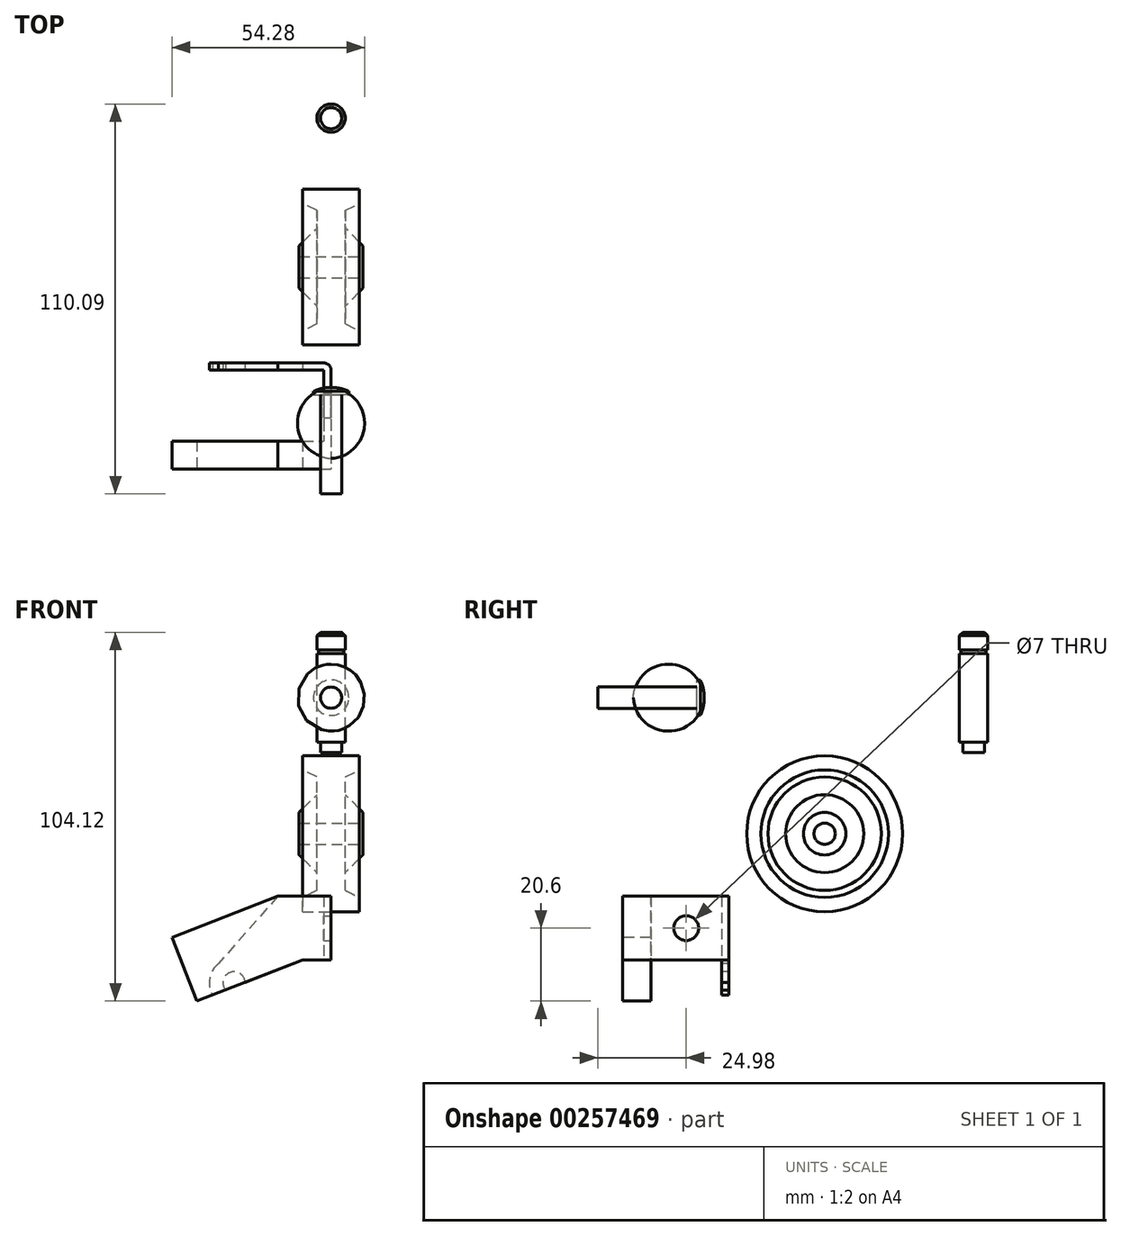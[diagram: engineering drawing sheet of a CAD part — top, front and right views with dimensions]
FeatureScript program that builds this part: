
annotation { "Feature Type Name" : "Feature", "Feature Type Description" : "" }
export const myFeature = defineFeature(function(context is Context, id is Id, definition is map)
    precondition{}
    {
        {
            var Q0;
            Q0=qCreatedBy(makeId("Front.planeOp"),FACE);
            var sketch = newSketch(context, id + "F0", { "sketchPlane" : qUnion([Q0])});
            skLineSegment(sketch, "E0", {"start": v(-8, 22) * mm, "end": v(8, 22) * mm});
            skLineSegment(sketch, "E1", {"start": v(-8, 22) * mm, "end": v(-8, 18) * mm});
            skLineSegment(sketch, "E2", {"start": v(8, 22) * mm, "end": v(8, 18) * mm});
            skLineSegment(sketch, "E3", {"start": v(-9, 3) * mm, "end": v(9, 3) * mm});
            skLineSegment(sketch, "E4", {"start": v(-9, 3) * mm, "end": v(-9, 6) * mm});
            skLineSegment(sketch, "E5", {"start": v(9, 3) * mm, "end": v(9, 6) * mm});
            skLineSegment(sketch, "E6", {"start": v(0, 0) * mm, "end": v(-4, 0) * mm});
            skLineSegment(sketch, "E7", {"start": v(0, 0) * mm, "end": v(4, 0) * mm});
            skLineSegment(sketch, "E8", {"start": v(-4, 11) * mm, "end": v(-4, 16) * mm});
            skLineSegment(sketch, "E9", {"start": v(4, 11) * mm, "end": v(4, 16) * mm});
            skLineSegment(sketch, "E10", {"start": v(-9, 6) * mm, "end": v(-4, 11) * mm});
            skLineSegment(sketch, "E11", {"start": v(-4, 16) * mm, "end": v(-8, 18) * mm});
            skLineSegment(sketch, "E12", {"start": v(4, 16) * mm, "end": v(8, 18) * mm});
            skLineSegment(sketch, "E13", {"start": v(4, 11) * mm, "end": v(9, 6) * mm});
            skSolve(sketch);
        }
        {
            var Q0;
            Q0=makeQuery(id+"F0.imprint","IMPRINT",FACE,{"disambiguationData":[TD([[makeQuery(id+"F0.imprint","IMPRINT",EDGE,{"derivedFrom":sQuery(id+"F0.wireOp",EDGE,"E0")}),-1.0]])]});
            var Q1;
            Q1=sQuery(id+"F0.wireOp",EDGE,"E6");
            revolve(context, id + "F1", {"entities" : qUnion([Q0]), "axis" : qUnion([Q1]), "revolveType" : RevolveType.FULL});
        }
        {
            var Q0;
            Q0=qCreatedBy(makeId("Right.planeOp"),FACE);
            var sketch = newSketch(context, id + "F2", { "sketchPlane" : qUnion([Q0])});
            skLineSegment(sketch, "E14", {"start": v(-64.05, 35.4) * mm, "end": v(-64.05, 38.4) * mm});
            skLineSegment(sketch, "E15", {"start": v(-64.05, 35.4) * mm, "end": v(-36.05, 35.4) * mm});
            skLineSegment(sketch, "E16", {"start": v(-64.05, 38.4) * mm, "end": v(-34.05, 38.4) * mm});
            skLineSegment(sketch, "E17", {"start": v(-36.08, 38.4) * mm, "end": v(-36.08, 33.4) * mm});
            skLineSegment(sketch, "E18", {"start": v(-36.08, 33.4) * mm, "end": v(-35.08, 33.4) * mm});
            skLineSegment(sketch, "E19", {"start": v(-36.08, 38.4) * mm, "end": v(-35.08, 38.4) * mm});
            skLineSegment(sketch, "E20", {"start": v(-35.08, 38.4) * mm, "end": v(-35.08, 33.4) * mm});
            skArc(sketch, "E21", {"start": v(-35.08, 33.4) * mm, "mid": v(-34.24, 35.83) * mm, "end": v(-34.05, 38.4) * mm});
            skSolve(sketch);
        }
        {
            var Q0;
            {var subQ2=sQuery(id+"F2.wireOp",EDGE,"E20");Q0=makeQuery(id+"F2.imprint","IMPRINT",FACE,{"disambiguationData":[TD([[makeQuery(id+"F2.imprint","IMPRINT",EDGE,{"derivedFrom":subQ2}),1.0]])]});}
            var Q1;
            {var subQ1=sQuery(id+"F2.wireOp",EDGE,"E18");Q1=makeQuery(id+"F2.imprint","IMPRINT",FACE,{"disambiguationData":[TD([[makeQuery(id+"F2.imprint","IMPRINT",EDGE,{"derivedFrom":subQ1}),1.0]])]});}
            var Q2;
            {var subQ0=sQuery(id+"F2.wireOp",EDGE,"E14");Q2=makeQuery(id+"F2.imprint","IMPRINT",FACE,{"disambiguationData":[TD([[makeQuery(id+"F2.imprint","IMPRINT",EDGE,{"derivedFrom":subQ0}),-1.0]])]});}
            var Q3;
            Q3=sQuery(id+"F2.wireOp",EDGE,"E16");
            revolve(context, id + "F3", {"entities" : qUnion([Q0, Q1, Q2]), "axis" : qUnion([Q3]), "revolveType" : RevolveType.FULL});
        }
        {
            var Q0;
            Q0=qCreatedBy(makeId("Right.planeOp"),FACE);
            var sketch = newSketch(context, id + "F4", { "sketchPlane" : qUnion([Q0])});
            skLineSegment(sketch, "E22", {"start": v(42.04, 56.87) * mm, "end": v(42.04, 22.87) * mm});
            skLineSegment(sketch, "E23", {"start": v(42.04, 22.87) * mm, "end": v(45.04, 22.87) * mm});
            skLineSegment(sketch, "E24", {"start": v(45.04, 22.87) * mm, "end": v(45.04, 25.87) * mm});
            skLineSegment(sketch, "E25", {"start": v(45.04, 25.87) * mm, "end": v(46.04, 25.87) * mm});
            skLineSegment(sketch, "E26", {"start": v(46.04, 25.87) * mm, "end": v(46.04, 50.87) * mm});
            skLineSegment(sketch, "E27", {"start": v(46.04, 50.87) * mm, "end": v(42.04, 50.87) * mm});
            skLineSegment(sketch, "E28", {"start": v(42.04, 50.87) * mm, "end": v(45.54, 50.87) * mm});
            skLineSegment(sketch, "E29", {"start": v(45.54, 50.87) * mm, "end": v(45.54, 51.87) * mm});
            skLineSegment(sketch, "E30", {"start": v(42.04, 51.87) * mm, "end": v(46.04, 51.87) * mm});
            skLineSegment(sketch, "E31", {"start": v(46.04, 51.87) * mm, "end": v(46.04, 55.87) * mm});
            skLineSegment(sketch, "E32", {"start": v(46.04, 55.87) * mm, "end": v(42.04, 55.87) * mm});
            skLineSegment(sketch, "E33", {"start": v(42.04, 56.87) * mm, "end": v(45.04, 56.87) * mm});
            skLineSegment(sketch, "E34", {"start": v(45.04, 56.87) * mm, "end": v(46.04, 55.87) * mm});
            skSolve(sketch);
        }
        {
            var Q0;
            Q0 = qSketchRegion(id + "F4", true);
            var Q1;
            Q1=sQuery(id+"F4.wireOp",EDGE,"E22");
            revolve(context, id + "F5", {"entities" : qUnion([Q0]), "axis" : qUnion([Q1]), "revolveType" : RevolveType.FULL});
        }
        {
            var Q0;
            Q0=qCreatedBy(makeId("Right.planeOp"),FACE);
            var sketch = newSketch(context, id + "F6", { "sketchPlane" : qUnion([Q0])});
            skLineSegment(sketch, "E35", {"start": v(-27.07, -17.65) * mm, "end": v(-51.07, -17.65) * mm});
            skLineSegment(sketch, "E36", {"start": v(-27.07, -17.65) * mm, "end": v(-27.07, -35.65) * mm});
            skLineSegment(sketch, "E37", {"start": v(-27.07, -35.65) * mm, "end": v(-51.07, -35.65) * mm});
            skLineSegment(sketch, "E38", {"start": v(-51.07, -35.65) * mm, "end": v(-51.07, -17.65) * mm});
            skLineSegment(sketch, "E39", {"start": v(-27.07, -17.65) * mm, "end": v(-29.07, -17.65) * mm});
            skLineSegment(sketch, "E40", {"start": v(-29.07, -17.65) * mm, "end": v(-29.07, -35.65) * mm});
            skLineSegment(sketch, "E41", {"start": v(-51.07, -17.65) * mm, "end": v(-49.07, -17.65) * mm});
            skLineSegment(sketch, "E42", {"start": v(-49.07, -17.65) * mm, "end": v(-49.07, -35.65) * mm});
            skSolve(sketch);
        }
        {
            var Q0;
            Q0=makeQuery(id+"F6.imprint","IMPRINT",FACE,{"disambiguationData":[TD([[makeQuery(id+"F6.imprint","IMPRINT",EDGE,{"derivedFrom":sQuery(id+"F6.wireOp",EDGE,"E35")}),1.0]])]});
            var Q1;
            {var subQ0=sQuery(id+"F6.wireOp",EDGE,"E36");Q1=makeQuery(id+"F6.imprint","IMPRINT",FACE,{"disambiguationData":[TD([[makeQuery(id+"F6.imprint","IMPRINT",EDGE,{"derivedFrom":subQ0}),-1.0]])]});}
            var Q2;
            {var subQ0=sQuery(id+"F6.wireOp",EDGE,"E38");Q2=makeQuery(id+"F6.imprint","IMPRINT",FACE,{"disambiguationData":[TD([[makeQuery(id+"F6.imprint","IMPRINT",EDGE,{"derivedFrom":subQ0}),-1.0]])]});}
            extrude(context, id + "F7", {"entities" : qUnion([Q0, Q1, Q2]), "oppositeDirection" : true, "depth" : 2 * mm});
        }
        {
            var Q0;
            Q0=makeQuery(id+"F7.opExtrude","CAP_FACE",FACE,{"disambiguationData":[OSD([sQuery(id+"F6.wireOp",EDGE,"E35"),sQuery(id+"F6.wireOp",EDGE,"E36"),sQuery(id+"F6.wireOp",EDGE,"E37"),sQuery(id+"F6.wireOp",EDGE,"E38"),sQuery(id+"F6.wireOp",EDGE,"E39"),sQuery(id+"F6.wireOp",EDGE,"E41")])],"isStart":false});
            var sketch = newSketch(context, id + "F8", { "sketchPlane" : qUnion([Q0])});
            skLineSegment(sketch, "E43.bottom", {"start": v(27.07, -17.65) * mm, "end": v(29.07, -17.65) * mm});
            skLineSegment(sketch, "E43.top", {"start": v(27.07, -35.65) * mm, "end": v(29.07, -35.65) * mm});
            skLineSegment(sketch, "E43.left", {"start": v(27.07, -17.65) * mm, "end": v(27.07, -35.65) * mm});
            skLineSegment(sketch, "E43.right", {"start": v(29.07, -17.65) * mm, "end": v(29.07, -35.65) * mm});
            skLineSegment(sketch, "E44.bottom", {"start": v(51.07, -17.65) * mm, "end": v(49.07, -17.65) * mm});
            skLineSegment(sketch, "E44.top", {"start": v(51.07, -35.65) * mm, "end": v(49.07, -35.65) * mm});
            skLineSegment(sketch, "E44.left", {"start": v(51.07, -17.65) * mm, "end": v(51.07, -35.65) * mm});
            skLineSegment(sketch, "E44.right", {"start": v(49.07, -17.65) * mm, "end": v(49.07, -35.65) * mm});
            skSolve(sketch);
        }
        {
            var Q0;
            Q0=makeQuery(id+"F8.imprint","IMPRINT",FACE,{"disambiguationData":[TD([[makeQuery(id+"F8.imprint","IMPRINT",EDGE,{"derivedFrom":sQuery(id+"F8.wireOp",EDGE,"E43.bottom")}),-1.0]])]});
            var Q1;
            Q1=makeQuery(id+"F8.imprint","IMPRINT",FACE,{"disambiguationData":[TD([[makeQuery(id+"F8.imprint","IMPRINT",EDGE,{"derivedFrom":sQuery(id+"F8.wireOp",EDGE,"E44.bottom")}),-1.0]])]});
            extrude(context, id + "F9", {"entities" : qUnion([Q0, Q1]), "operationType" : NewBodyOperationType.ADD, "depth" : 13 * mm});
        }
        {
            var Q0;
            Q0=makeQuery(id+"F9.boolean.opBoolean","MERGE",FACE,{"derivedFrom":[makeQuery(id+"F7.opExtrude","SWEPT_FACE",FACE,{"disambiguationData":[OSD([sQuery(id+"F6.wireOp",EDGE,"E38")])]}),makeQuery(id+"F9.opExtrude","SWEPT_FACE",FACE,{"disambiguationData":[OSD([sQuery(id+"F8.wireOp",EDGE,"E44.left")])]})]});
            var sketch = newSketch(context, id + "F10", { "sketchPlane" : qUnion([Q0])});
            skLineSegment(sketch, "E45", {"start": v(0, -35.65) * mm, "end": v(-8, -35.65) * mm});
            skLineSegment(sketch, "E46", {"start": v(-8, -35.65) * mm, "end": v(-15, -17.65) * mm});
            skSolve(sketch);
        }
        {
            var Q0;
            {var subQ0=sQuery(id+"F10.wireOp",EDGE,"E46");Q0=makeQuery(id+"F10.imprint","IMPRINT",FACE,{"disambiguationData":[TD([[makeQuery(id+"F10.imprint","IMPRINT",EDGE,{"derivedFrom":subQ0}),1.0]])]});}
            extrude(context, id + "F11", {"entities" : qUnion([Q0]), "operationType" : NewBodyOperationType.REMOVE, "oppositeDirection" : true, "depth" : 24 * mm});
        }
        {
            var Q0;
            Q0=makeQuery(id+"F11.boolean.opBoolean","COPY",FACE,{"disambiguationData":[TD([makeQuery(id+"F7.opExtrude","SWEPT_FACE",FACE,{"disambiguationData":[OSD([sQuery(id+"F6.wireOp",EDGE,"E36")])]})])],"derivedFrom":makeQuery(id+"F11.opExtrude","SWEPT_FACE",FACE,{"disambiguationData":[OSD([sQuery(id+"F10.wireOp",EDGE,"E46")])]})});
            var Q1;
            Q1=makeQuery(id+"F11.boolean.opBoolean","COPY",FACE,{"disambiguationData":[TD([makeQuery(id+"F7.opExtrude","SWEPT_FACE",FACE,{"disambiguationData":[OSD([sQuery(id+"F6.wireOp",EDGE,"E38")])]})])],"derivedFrom":makeQuery(id+"F11.opExtrude","SWEPT_FACE",FACE,{"disambiguationData":[OSD([sQuery(id+"F10.wireOp",EDGE,"E46")])]})});
            extrude(context, id + "F12", {"entities" : qUnion([Q0, Q1]), "operationType" : NewBodyOperationType.ADD, "depth" : 32 * mm});
        }
        {
            var Q0;
            {var subQ0=sQuery(id+"F8.wireOp",EDGE,"E44.top");var subQ1=sQuery(id+"F6.wireOp",EDGE,"E38");var subQ2=sQuery(id+"F6.wireOp",EDGE,"E37");var subQ3=sQuery(id+"F8.wireOp",EDGE,"E44.left");var subQ4=sQuery(id+"F10.wireOp",EDGE,"E46");var subQ5=sQuery(id+"F10.wireOp",EDGE,"E45");Q0=makeQuery(id+"F12.opExtrude","SWEPT_FACE",FACE,{"disambiguationData":[OSD([subQ2,subQ1,subQ0,subQ3,subQ5,subQ4]),TDD([makeQuery(id+"F11.boolean.opBoolean","COPY",EDGE,{"disambiguationData":[TD([makeQuery(id+"F7.opExtrude","SWEPT_FACE",FACE,{"disambiguationData":[OSD([subQ1])]})])],"derivedFrom":makeQuery(id+"F11.opExtrude","SWEPT_EDGE",EDGE,{"disambiguationData":[OSD([subQ2,subQ1,subQ0,subQ3,subQ5,subQ4])]})})])]});}
            var Q1;
            {var subQ0=sQuery(id+"F6.wireOp",EDGE,"E37");var subQ1=sQuery(id+"F8.wireOp",EDGE,"E44.top");var subQ2=sQuery(id+"F10.wireOp",EDGE,"E46");var subQ3=sQuery(id+"F10.wireOp",EDGE,"E45");var subQ4=sQuery(id+"F8.wireOp",EDGE,"E44.left");var subQ5=sQuery(id+"F6.wireOp",EDGE,"E38");Q1=makeQuery(id+"F12.opExtrude","SWEPT_FACE",FACE,{"disambiguationData":[OSD([subQ0,subQ5,subQ1,subQ4,subQ3,subQ2]),TDD([makeQuery(id+"F11.boolean.opBoolean","COPY",EDGE,{"disambiguationData":[TD([makeQuery(id+"F7.opExtrude","SWEPT_FACE",FACE,{"disambiguationData":[OSD([sQuery(id+"F6.wireOp",EDGE,"E36")])]})])],"derivedFrom":makeQuery(id+"F11.opExtrude","SWEPT_EDGE",EDGE,{"disambiguationData":[OSD([subQ0,subQ5,subQ1,subQ4,subQ3,subQ2])]})})])]});}
            extrude(context, id + "F13", {"entities" : qUnion([Q0, Q1]), "operationType" : NewBodyOperationType.ADD, "depth" : 6 * mm});
        }
        {
            var Q0;
            {var subQ0=sQuery(id+"F10.wireOp",EDGE,"E46");Q0=makeQuery(id+"F12.boolean.opBoolean","MERGE",FACE,{"derivedFrom":[makeQuery(id+"F9.boolean.opBoolean","MERGE",FACE,{"derivedFrom":[makeQuery(id+"F7.opExtrude","SWEPT_FACE",FACE,{"disambiguationData":[OSD([sQuery(id+"F6.wireOp",EDGE,"E38")])]}),makeQuery(id+"F9.opExtrude","SWEPT_FACE",FACE,{"disambiguationData":[OSD([sQuery(id+"F8.wireOp",EDGE,"E44.left")])]})]}),makeQuery(id+"F12.opExtrude","SWEPT_FACE",FACE,{"disambiguationData":[OSD([subQ0]),TDD([makeQuery(id+"F11.boolean.opBoolean","COPY",EDGE,{"derivedFrom":makeQuery(id+"F11.opExtrude","CAP_EDGE",EDGE,{"disambiguationData":[OSD([subQ0])],"isStart":true})})])]})]});}
            var sketch = newSketch(context, id + "F14", { "sketchPlane" : qUnion([Q0])});
            skPoint(sketch, "E47.first.point", {"position": v(-40.24, -41.04) * mm});
            skPoint(sketch, "E47.third.point", {"position": v(-30.84, -29.93) * mm});
            skLineSegment(sketch, "E48", {"start": v(-15, -17.65) * mm, "end": v(-31.73, -36.63) * mm});
            skLineSegment(sketch, "E49", {"start": v(-8, -35.65) * mm, "end": v(-22.05, -46.58) * mm});
            skCircle(sketch, "E50", {"center": v(-27.38, -42.09) * mm, "radius": 6.98 * mm});
            skPoint(sketch, "E50.third.point", {"position": v(-21.22, -38.82) * mm});
            skCircle(sketch, "E51", {"center": v(-27.38, -42.09) * mm, "radius": 3.12 * mm});
            skSolve(sketch);
        }
        {
            var Q0;
            {var subQ4=sQuery(id+"F14.wireOp",EDGE,"E48");Q0=makeQuery(id+"F14.imprint","IMPRINT",FACE,{"disambiguationData":[TD([[makeQuery(id+"F14.imprint","IMPRINT",EDGE,{"derivedFrom":subQ4}),-1.0]])]});}
            var Q1;
            Q1=makeQuery(id+"F14.imprint","IMPRINT",FACE,{"disambiguationData":[TD([[makeQuery(id+"F14.imprint","IMPRINT",EDGE,{"derivedFrom":sQuery(id+"F14.wireOp",EDGE,"E51")}),1.0]])]});
            extrude(context, id + "F15", {"entities" : qUnion([Q0, Q1]), "operationType" : NewBodyOperationType.REMOVE, "oppositeDirection" : true, "depth" : 24 * mm});
        }
        {
            var Q0;
            Q0=makeQuery(id+"F7.opExtrude","CAP_FACE",FACE,{"disambiguationData":[OSD([sQuery(id+"F6.wireOp",EDGE,"E35"),sQuery(id+"F6.wireOp",EDGE,"E36"),sQuery(id+"F6.wireOp",EDGE,"E37"),sQuery(id+"F6.wireOp",EDGE,"E38"),sQuery(id+"F6.wireOp",EDGE,"E39"),sQuery(id+"F6.wireOp",EDGE,"E41")])],"isStart":true});
            var sketch = newSketch(context, id + "F16", { "sketchPlane" : qUnion([Q0])});
            skLineSegment(sketch, "E52", {"start": v(-27.07, -17.65) * mm, "end": v(-39.07, -17.65) * mm});
            skLineSegment(sketch, "E53", {"start": v(-39.07, -17.65) * mm, "end": v(-39.07, -26.65) * mm});
            skCircle(sketch, "E54", {"center": v(-39.07, -26.65) * mm, "radius": 3.5 * mm});
            skSolve(sketch);
        }
        {
            var Q0;
            Q0=makeQuery(id+"F16.imprint","IMPRINT",FACE,{"disambiguationData":[TD([[makeQuery(id+"F16.imprint","IMPRINT",EDGE,{"derivedFrom":sQuery(id+"F16.wireOp",EDGE,"E54")}),1.0]])]});
            extrude(context, id + "F17", {"entities" : qUnion([Q0]), "operationType" : NewBodyOperationType.REMOVE, "oppositeDirection" : true, "depth" : 2 * mm});
        }
        {
            var Q0;
            Q0=makeQuery(id+"F7.opExtrude","CAP_EDGE",EDGE,{"disambiguationData":[OSD([sQuery(id+"F6.wireOp",EDGE,"E38")])],"isStart":true});
            var Q1;
            Q1=makeQuery(id+"F7.opExtrude","CAP_EDGE",EDGE,{"disambiguationData":[OSD([sQuery(id+"F6.wireOp",EDGE,"E36")])],"isStart":true});
            var Q2;
            Q2=makeQuery(id+"F9.opExtrude","CAP_EDGE",EDGE,{"disambiguationData":[OSD([sQuery(id+"F8.wireOp",EDGE,"E44.right")])],"isStart":true});
            var Q3;
            Q3=makeQuery(id+"F9.opExtrude","CAP_EDGE",EDGE,{"disambiguationData":[OSD([sQuery(id+"F8.wireOp",EDGE,"E43.right")])],"isStart":true});
            fillet(context, id + "F18", {"entities" : qUnion([Q0, Q1, Q2, Q3]), "radius" : 2 * mm, "tangentPropagation" : true, "allowEdgeOverflow" : false});
        }
    });
